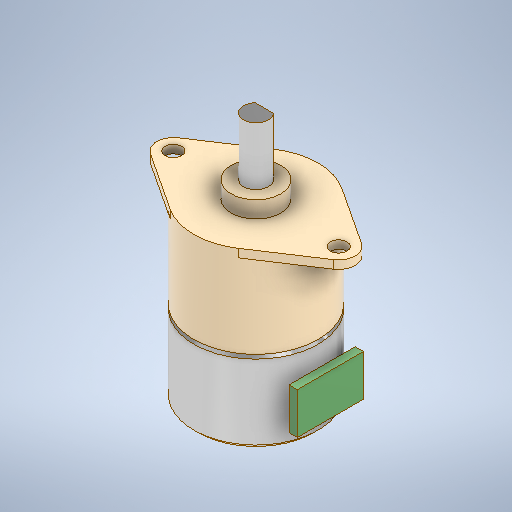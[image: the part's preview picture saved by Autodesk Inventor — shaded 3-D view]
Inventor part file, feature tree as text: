
AUTODESK INVENTOR PART (.ipt)
format: ipt  version: 2025.3 (Build 293356000, 356)  size: 338,944 bytes
history: native  units: mm
features: sketch x8, extrude x6, other x2, revolve x1
ambient origin geometry x8: Origin, YZ Plane, XZ Plane, XY Plane, X Axis, Y Axis, Z Axis, Center Point
bodies: Body1 (feature_tree)
feature tree (17):
  other  "ソリッド1"
  revolve  "回転1"
  sketch  "スケッチ3"
  extrude  "押し出し1"  Depth=7.5mm
  extrude  "押し出し2"  Depth=10.0mm
  extrude  "押し出し3"  TaperAngle=135.0deg  [1 undecoded]
  extrude  "押し出し4"  Depth=0.5mm
  extrude  "押し出し5"  TaperAngle=90.0deg  [1 undecoded]
  other  "作業平面1"
  extrude  "押し出し6"  Depth=11.0mm TaperAngle=0.0deg
  sketch  "スケッチ2"
  sketch  "スケッチ4"
  sketch  "スケッチ5"
  sketch  "スケッチ6"
  sketch  "スケッチ7"
  sketch  "スケッチ8"
  sketch  "スケッチ9"
note: 2 required parameter values undecoded (feature->parameter linkage not recoverable at this tier; creation-order binding heuristic only, values carry confidence <= 0.55)
